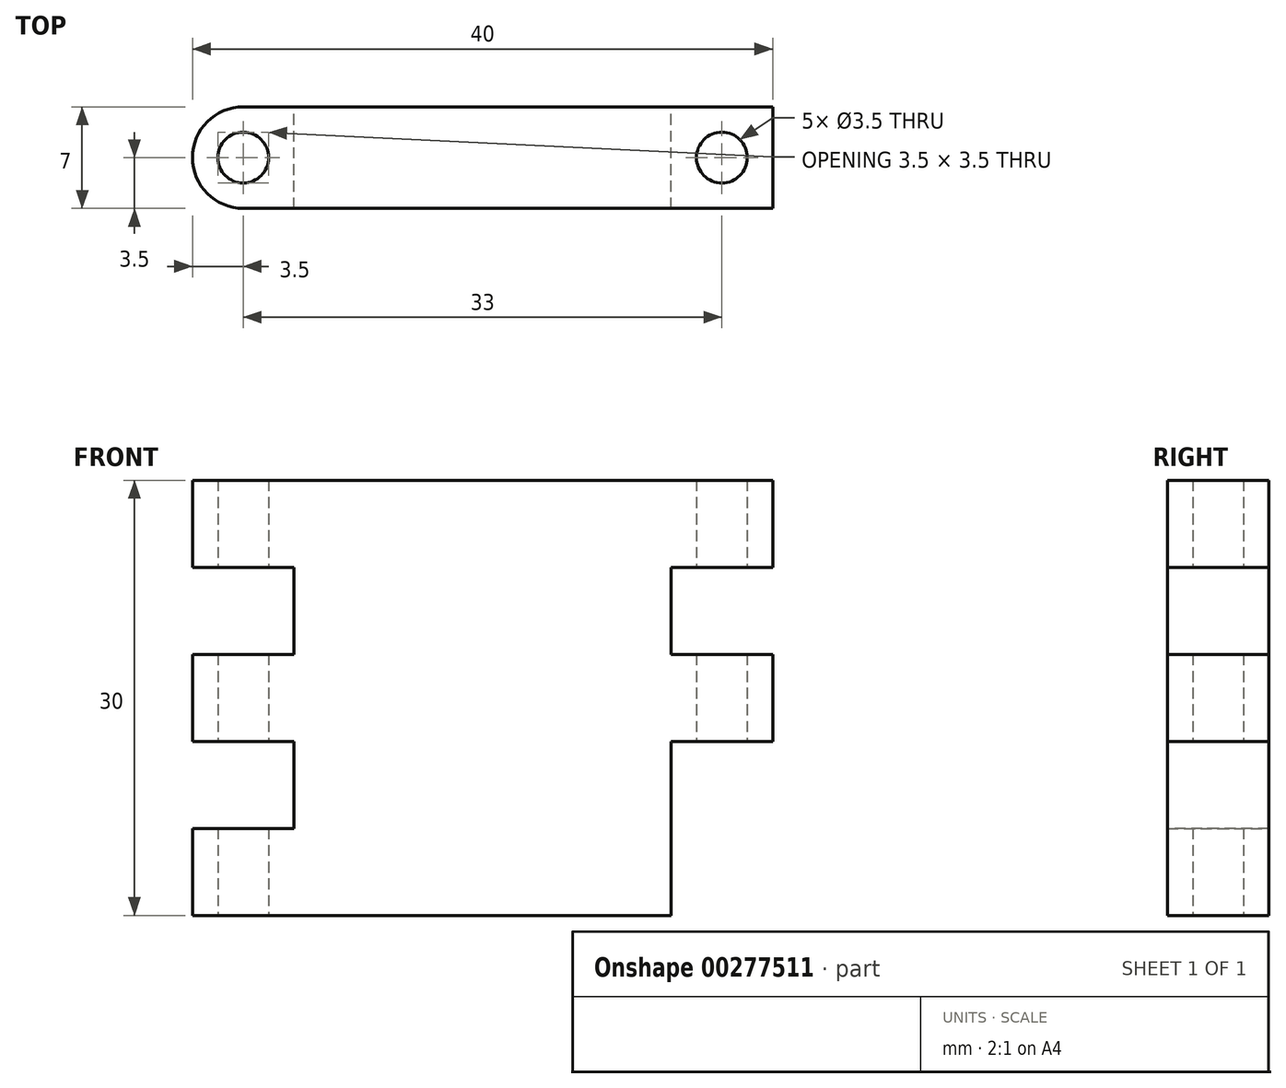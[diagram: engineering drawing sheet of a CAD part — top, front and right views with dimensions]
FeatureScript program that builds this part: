
annotation { "Feature Type Name" : "Feature", "Feature Type Description" : "" }
export const myFeature = defineFeature(function(context is Context, id is Id, definition is map)
    precondition{}
    {
        {
            var Q0;
            Q0=qCreatedBy(makeId("Front.planeOp"),FACE);
            var sketch = newSketch(context, id + "F0", { "sketchPlane" : qUnion([Q0])});
            skLineSegment(sketch, "E0.bottom", {"start": v(20, 15) * mm, "end": v(-20, 15) * mm});
            skLineSegment(sketch, "E0.top", {"start": v(20, -15) * mm, "end": v(-20, -15) * mm});
            skLineSegment(sketch, "E0.left", {"start": v(20, 15) * mm, "end": v(20, -15) * mm});
            skLineSegment(sketch, "E0.right", {"start": v(-20, 15) * mm, "end": v(-20, -15) * mm});
            skPoint(sketch, "E0.middle", {"position": v(0, 0) * mm});
            skPoint(sketch, "E1", {"position": v(-20, -9) * mm});
            skPoint(sketch, "E2", {"position": v(-20, -3) * mm});
            skPoint(sketch, "E3", {"position": v(-20, 3) * mm});
            skPoint(sketch, "E4", {"position": v(-20, 9) * mm});
            skLineSegment(sketch, "E5", {"start": v(-13, 15) * mm, "end": v(-13, -15) * mm});
            skLineSegment(sketch, "E6", {"start": v(-20, 9) * mm, "end": v(-13, 9) * mm});
            skLineSegment(sketch, "E7", {"start": v(-20, 3) * mm, "end": v(-13, 3) * mm});
            skLineSegment(sketch, "E8", {"start": v(-20, -3) * mm, "end": v(-13, -3) * mm});
            skLineSegment(sketch, "E9", {"start": v(-20, -9) * mm, "end": v(-13, -9) * mm});
            skLineSegment(sketch, "E10", {"start": v(13, 15) * mm, "end": v(13, -15) * mm});
            skPoint(sketch, "E11", {"position": v(13, -9) * mm});
            skPoint(sketch, "E11.positionSnap0", {"position": v(-16.5, -9) * mm});
            skPoint(sketch, "E12", {"position": v(13, -3) * mm});
            skPoint(sketch, "E13", {"position": v(13, 3) * mm});
            skPoint(sketch, "E14", {"position": v(13, 9) * mm});
            skLineSegment(sketch, "E15", {"start": v(13, 9) * mm, "end": v(20, 9) * mm});
            skLineSegment(sketch, "E16", {"start": v(13, 3) * mm, "end": v(20, 3) * mm});
            skLineSegment(sketch, "E17", {"start": v(13, -3) * mm, "end": v(20, -3) * mm});
            skLineSegment(sketch, "E18", {"start": v(13, -9) * mm, "end": v(20, -9) * mm});
            skLineSegment(sketch, "E19", {"start": v(20, -9) * mm, "end": v(13, -9) * mm});
            skSolve(sketch);
        }
        {
            var Q0;
            {var subQ5=sQuery(id+"F0.wireOp",EDGE,"E15");Q0=makeQuery(id+"F0.imprint","IMPRINT",FACE,{"disambiguationData":[TD([[makeQuery(id+"F0.imprint","IMPRINT",EDGE,{"derivedFrom":subQ5}),1.0]])]});}
            var Q1;
            {var subQ5=sQuery(id+"F0.wireOp",EDGE,"E19");Q1=makeQuery(id+"F0.imprint","IMPRINT",FACE,{"disambiguationData":[TD([[makeQuery(id+"F0.imprint","IMPRINT",EDGE,{"derivedFrom":subQ5}),1.0]])]});}
            var Q2;
            {var subQ0=sQuery(id+"F0.wireOp",EDGE,"E16");Q2=makeQuery(id+"F0.imprint","IMPRINT",FACE,{"disambiguationData":[TD([[makeQuery(id+"F0.imprint","IMPRINT",EDGE,{"derivedFrom":subQ0}),-1.0]])]});}
            var Q3;
            {var subQ5=sQuery(id+"F0.wireOp",EDGE,"E6");Q3=makeQuery(id+"F0.imprint","IMPRINT",FACE,{"disambiguationData":[TD([[makeQuery(id+"F0.imprint","IMPRINT",EDGE,{"derivedFrom":subQ5}),1.0]])]});}
            var Q4;
            {var subQ0=sQuery(id+"F0.wireOp",EDGE,"E7");Q4=makeQuery(id+"F0.imprint","IMPRINT",FACE,{"disambiguationData":[TD([[makeQuery(id+"F0.imprint","IMPRINT",EDGE,{"derivedFrom":subQ0}),-1.0]])]});}
            var Q5;
            {var subQ5=sQuery(id+"F0.wireOp",EDGE,"E9");Q5=makeQuery(id+"F0.imprint","IMPRINT",FACE,{"disambiguationData":[TD([[makeQuery(id+"F0.imprint","IMPRINT",EDGE,{"derivedFrom":subQ5}),-1.0]])]});}
            var Q6;
            {var subQ4=sQuery(id+"F0.wireOp",EDGE,"E5");var subQ10=sQuery(id+"F0.wireOp",EDGE,"E0.bottom");var subQ12=makeQuery(id+"F0.imprint","INTERSECT",VERTEX,{"derivedFrom":[subQ10,subQ4]});Q6=makeQuery(id+"F0.imprint","IMPRINT",FACE,{"disambiguationData":[TD([[makeQuery(id+"F0.imprint","IMPRINT",EDGE,{"disambiguationData":[TD([[subQ12,1.0]])],"derivedFrom":subQ10}),1.0]])]});}
            extrude(context, id + "F1", {"entities" : qUnion([Q0, Q1, Q2, Q3, Q4, Q5, Q6]), "depth" : 7 * mm});
        }
        {
            var Q0;
            Q0=makeQuery(id+"F1.opExtrude","SWEPT_FACE",FACE,{"disambiguationData":[OSD([sQuery(id+"F0.wireOp",EDGE,"E0.top")])]});
            var sketch = newSketch(context, id + "F2", { "sketchPlane" : qUnion([Q0])});
            skCircle(sketch, "E20", {"center": v(-16.5, 3.5) * mm, "radius": 1.75 * mm});
            skCircle(sketch, "E21", {"center": v(-16.5, 3.5) * mm, "radius": 3.5 * mm});
            skCircle(sketch, "E22", {"center": v(16.5, 3.5) * mm, "radius": 3.5 * mm});
            skCircle(sketch, "E23", {"center": v(16.5, 3.5) * mm, "radius": 1.75 * mm});
            skSolve(sketch);
        }
        {
            var Q0;
            Q0=makeQuery(id+"F2.imprint","IMPRINT",FACE,{"disambiguationData":[TD([[makeQuery(id+"F2.imprint","IMPRINT",EDGE,{"derivedFrom":sQuery(id+"F2.wireOp",EDGE,"E20")}),1.0]])]});
            var Q1;
            Q1 = qSketchRegion(id + "F4", true);
            var Q2;
            {var subQ0=sQuery(id+"F2.wireOp",EDGE,"E21");var subQ1=sQuery(id+"F0.wireOp",EDGE,"E0.top");var subQ4=makeQuery(id+"F1.opExtrude","CAP_EDGE",EDGE,{"disambiguationData":[OSD([subQ1])],"isStart":true});var subQ5=makeQuery(id+"F2.imprint","INTERSECT",VERTEX,{"derivedFrom":[subQ4,subQ0]});Q2=makeQuery(id+"F2.imprint","IMPRINT",FACE,{"disambiguationData":[TD([[makeQuery(id+"F2.imprint","IMPRINT",EDGE,{"disambiguationData":[TD([[subQ5,1.0]])],"derivedFrom":subQ0}),-1.0]])]});}
            var Q3;
            {var subQ0=sQuery(id+"F2.wireOp",EDGE,"E21");var subQ1=sQuery(id+"F0.wireOp",EDGE,"E0.top");var subQ4=makeQuery(id+"F1.opExtrude","CAP_EDGE",EDGE,{"disambiguationData":[OSD([subQ1])],"isStart":false});var subQ5=makeQuery(id+"F2.imprint","INTERSECT",VERTEX,{"derivedFrom":[subQ4,subQ0]});Q3=makeQuery(id+"F2.imprint","IMPRINT",FACE,{"disambiguationData":[TD([[makeQuery(id+"F2.imprint","IMPRINT",EDGE,{"disambiguationData":[TD([[subQ5,-1.0]])],"derivedFrom":subQ0}),-1.0]])]});}
            var Q4;
            {var subQ0=sQuery(id+"F2.wireOp",EDGE,"E22");var subQ1=sQuery(id+"F0.wireOp",EDGE,"E0.top");var subQ2=makeQuery(id+"F1.opExtrude","CAP_EDGE",EDGE,{"disambiguationData":[OSD([subQ1])],"isStart":false});var subQ3=makeQuery(id+"F2.imprint","INTERSECT",VERTEX,{"derivedFrom":[subQ2,subQ0]});Q4=makeQuery(id+"F2.imprint","IMPRINT",FACE,{"disambiguationData":[TD([[makeQuery(id+"F2.imprint","IMPRINT",EDGE,{"disambiguationData":[TD([[subQ3,1.0]])],"derivedFrom":subQ0}),-1.0]])]});}
            var Q5;
            {var subQ0=sQuery(id+"F2.wireOp",EDGE,"E22");var subQ1=sQuery(id+"F0.wireOp",EDGE,"E0.top");var subQ4=makeQuery(id+"F1.opExtrude","CAP_EDGE",EDGE,{"disambiguationData":[OSD([subQ1])],"isStart":true});var subQ5=makeQuery(id+"F2.imprint","INTERSECT",VERTEX,{"derivedFrom":[subQ4,subQ0]});Q5=makeQuery(id+"F2.imprint","IMPRINT",FACE,{"disambiguationData":[TD([[makeQuery(id+"F2.imprint","IMPRINT",EDGE,{"disambiguationData":[TD([[subQ5,-1.0]])],"derivedFrom":subQ0}),-1.0]])]});}
            var Q6;
            Q6=makeQuery(id+"F2.imprint","IMPRINT",FACE,{"disambiguationData":[TD([[makeQuery(id+"F2.imprint","IMPRINT",EDGE,{"derivedFrom":sQuery(id+"F2.wireOp",EDGE,"E23")}),1.0]])]});
            extrude(context, id + "F3", {"entities" : qUnion([Q0, Q1, Q2, Q3, Q4, Q5, Q6]), "operationType" : NewBodyOperationType.REMOVE, "endBound" : BoundingType.THROUGH_ALL, "oppositeDirection" : true, "depth" : 25 * mm});
        }
    });
